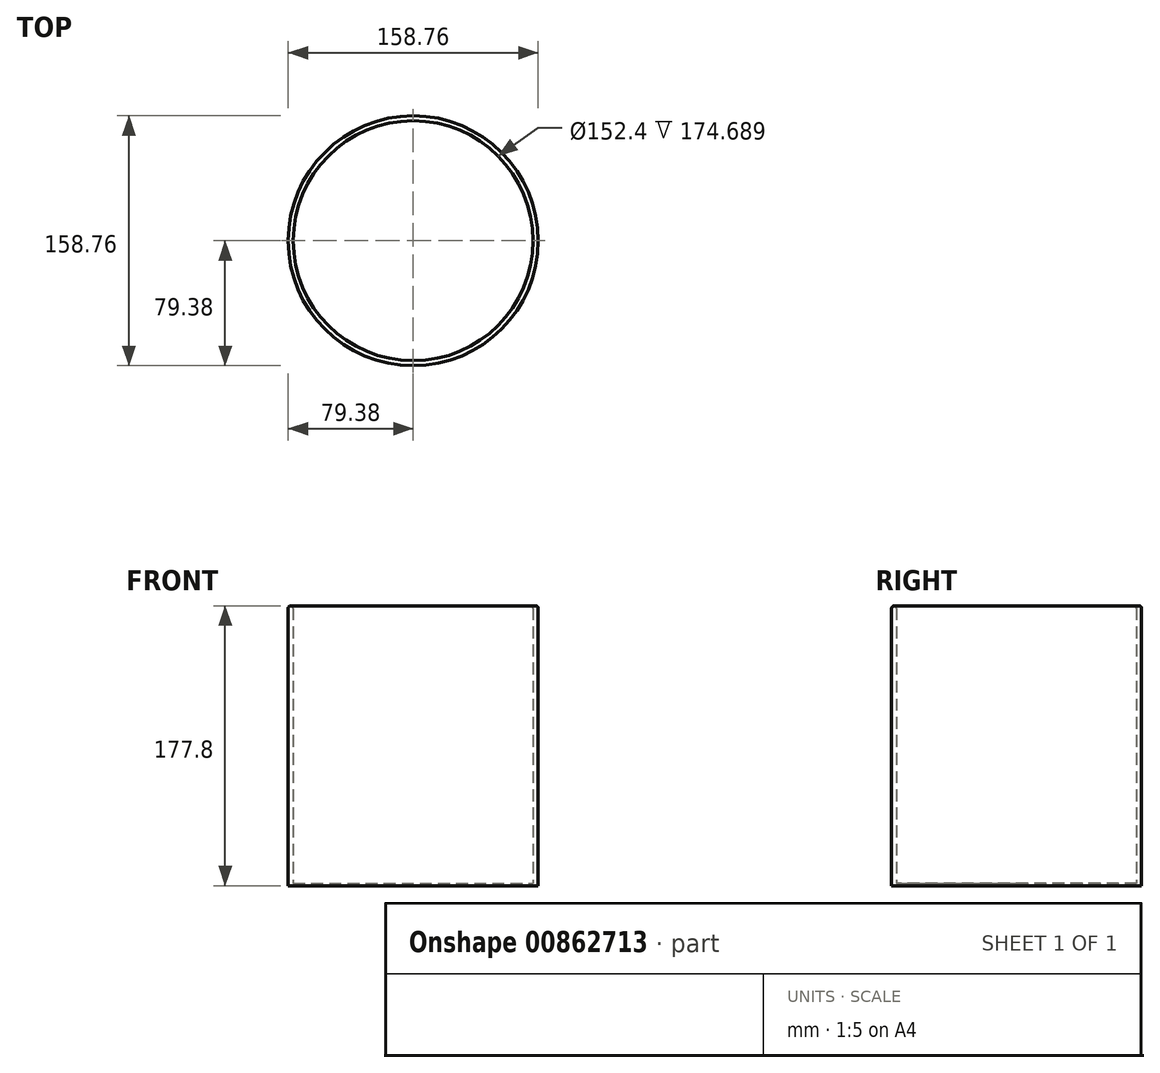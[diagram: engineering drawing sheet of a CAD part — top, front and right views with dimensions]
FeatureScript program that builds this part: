
annotation { "Feature Type Name" : "Feature", "Feature Type Description" : "" }
export const myFeature = defineFeature(function(context is Context, id is Id, definition is map)
    precondition{}
    {
        {
            var Q0;
            Q0=qCreatedBy(makeId("Front.planeOp"),FACE);
            var sketch = newSketch(context, id + "F0", { "sketchPlane" : qUnion([Q0])});
            skLineSegment(sketch, "E0", {"start": v(0, 0) * mm, "end": v(-79.38, 0) * mm});
            skLineSegment(sketch, "E1", {"start": v(-79.38, 0) * mm, "end": v(-79.38, 177.8) * mm});
            skArc(sketch, "E2", {"start": v(-76.2, 176.21) * mm, "mid": v(-77.79, 177.8) * mm, "end": v(-79.38, 176.21) * mm});
            skLineSegment(sketch, "E3", {"start": v(0, 0) * mm, "end": v(0, 1.52) * mm});
            skLineSegment(sketch, "E4", {"start": v(0, 1.52) * mm, "end": v(-76.2, 1.52) * mm});
            skLineSegment(sketch, "E5", {"start": v(-76.2, 1.52) * mm, "end": v(-76.2, 176.21) * mm});
            skLineSegment(sketch, "E6", {"start": v(0, 1.52) * mm, "end": v(0, 77.72) * mm, "construction": true});
            skSolve(sketch);
        }
        {
            var Q0;
            {var subQ2=sQuery(id+"F0.wireOp",EDGE,"E0");Q0=makeQuery(id+"F0.imprint","IMPRINT",FACE,{"disambiguationData":[TD([[makeQuery(id+"F0.imprint","IMPRINT",EDGE,{"derivedFrom":subQ2}),-1.0]])]});}
            var Q1;
            Q1=sQuery(id+"F0.wireOp",EDGE,"E6");
            revolve(context, id + "F1", {"surfaceOperationType" : NewSurfaceOperationType.NEW, "entities" : qUnion([Q0]), "axis" : qUnion([Q1]), "revolveType" : RevolveType.FULL});
        }
    });
